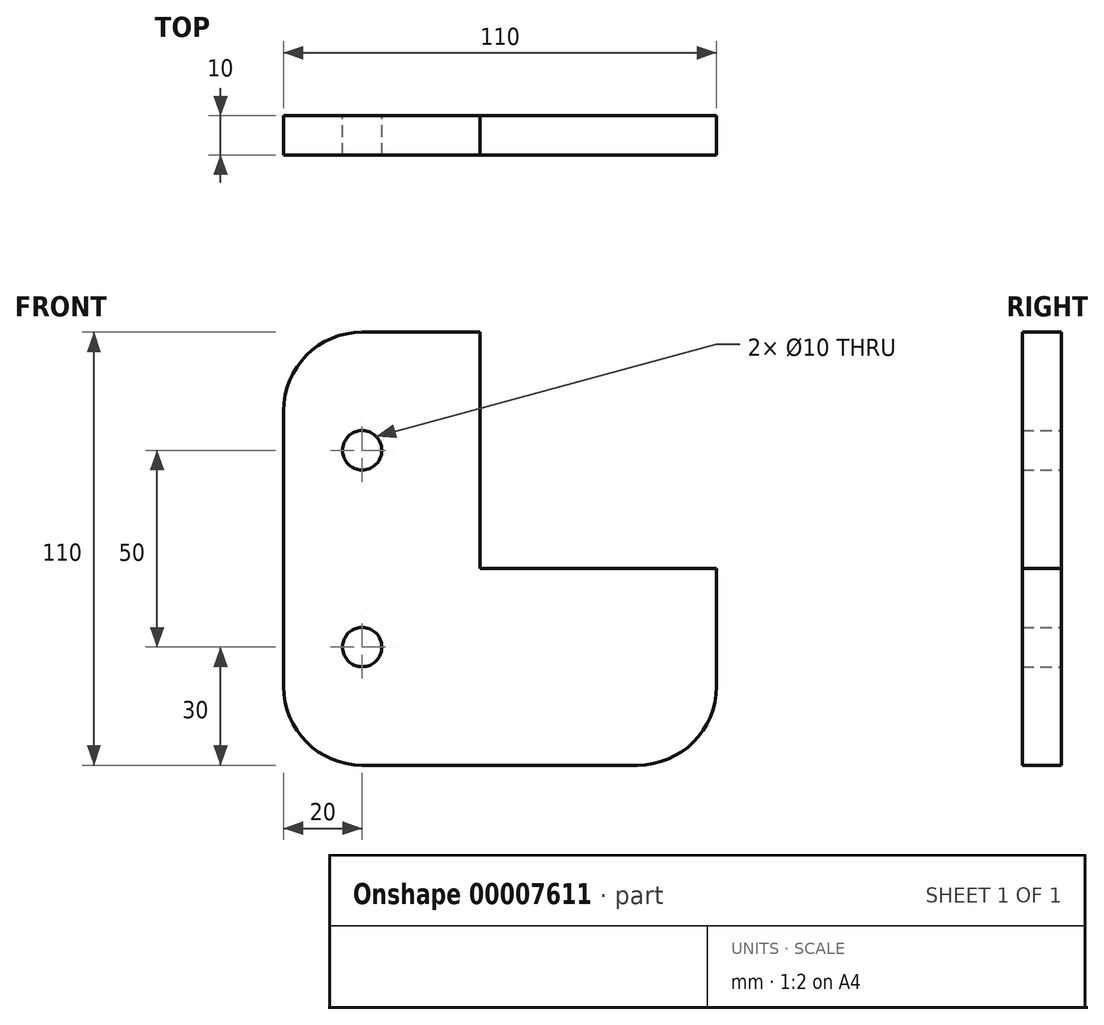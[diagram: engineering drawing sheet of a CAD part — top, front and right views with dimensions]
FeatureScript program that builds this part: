
annotation { "Feature Type Name" : "Feature", "Feature Type Description" : "" }
export const myFeature = defineFeature(function(context is Context, id is Id, definition is map)
    precondition{}
    {
        {
            var Q0;
            Q0=qCreatedBy(makeId("Front.planeOp"),FACE);
            var sketch = newSketch(context, id + "F0", { "sketchPlane" : qUnion([Q0])});
            skLineSegment(sketch, "E0", {"start": v(0, 0) * mm, "end": v(0, 60) * mm});
            skLineSegment(sketch, "E1", {"start": v(0, 60) * mm, "end": v(-30, 60) * mm});
            skLineSegment(sketch, "E2", {"start": v(-50, 40) * mm, "end": v(-50, -30) * mm});
            skLineSegment(sketch, "E3", {"start": v(-30, -50) * mm, "end": v(40, -50) * mm});
            skLineSegment(sketch, "E4", {"start": v(60, -30) * mm, "end": v(60, 0) * mm});
            skLineSegment(sketch, "E5", {"start": v(60, 0) * mm, "end": v(0, 0) * mm});
            skPoint(sketch, "E6.visualSharp", {"position": v(-50, 60) * mm});
            skArc(sketch, "E6.filletArc", {"start": v(-30, 60) * mm, "mid": v(-44.14, 54.14) * mm, "end": v(-50, 40) * mm});
            skPoint(sketch, "E7.visualSharp", {"position": v(-50, -50) * mm});
            skArc(sketch, "E7.filletArc", {"start": v(-50, -30) * mm, "mid": v(-44.14, -44.14) * mm, "end": v(-30, -50) * mm});
            skPoint(sketch, "E8.visualSharp", {"position": v(60, -50) * mm});
            skArc(sketch, "E8.filletArc", {"start": v(40, -50) * mm, "mid": v(54.14, -44.14) * mm, "end": v(60, -30) * mm});
            skCircle(sketch, "E9", {"center": v(-30, 30) * mm, "radius": 5 * mm});
            skCircle(sketch, "E10", {"center": v(-30, -20) * mm, "radius": 5 * mm});
            skSolve(sketch);
        }
        {
            var Q0;
            Q0 = qSketchRegion(id + "F0", true);
            extrude(context, id + "F1", {"entities" : qUnion([Q0]), "endBound" : BoundingType.SYMMETRIC, "depth" : 10 * mm});
        }
    });
